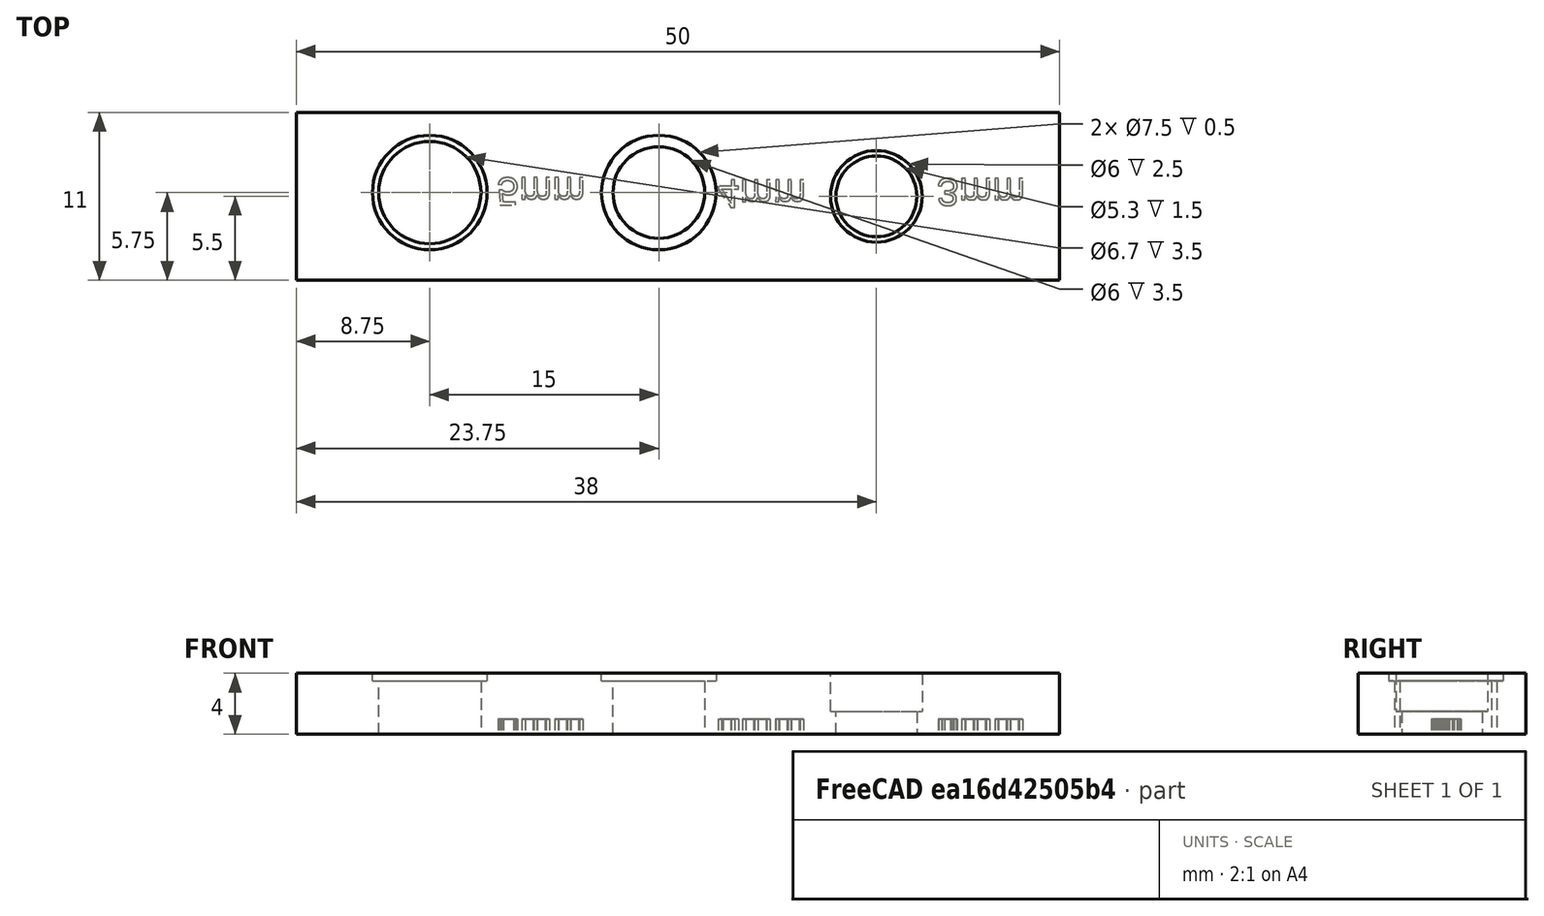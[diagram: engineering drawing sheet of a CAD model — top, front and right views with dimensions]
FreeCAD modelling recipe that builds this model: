
FCSTD DOCUMENT  (FreeCAD 0.17R13522 (Git))
Label: test_for_leds
License: CreativeCommons Attribution-ShareAlike
LicenseURL: http://creativecommons.org/licenses/by-sa/4.0/
objects: Part::Cut×6, Part::Feature×3, Part::Part2DObjectPython×3, Part::Extrusion×3, Part::Box×1
note: 16 computed .brp shape members not serialized (recipe doc carries the construction recipe); baked Part::Feature solids carry a one-line shape summary decoded from their .brp

FEATURE [Part::Box] Box  label="Cube"
  AttacherType = Attacher::AttachEngine3D
  Height = 4
  Length = 50
  Width = 11
FEATURE [Part::Feature] Fusion001001  label="perforador led 5 mm001"
  Placement = pos=(5,2,4) rot=(0,0,1;0rad)
  shape: bbox 7.5 x 7.5 x 10 mm, 13 faces (baked)
FEATURE [Part::Feature] Fusion001002  label="perforador led 4 mm001"
  Placement = pos=(20,2,4) rot=(0,0,1;0rad)
  shape: bbox 7.5 x 7.5 x 10 mm, 13 faces (baked)
FEATURE [Part::Feature] Fusion001003  label="perforador led 3 mm001"
  Placement = pos=(35,2.5,4) rot=(0,0,1;0rad)
  shape: bbox 6 x 6 x 10 mm, 13 faces (baked)
FEATURE [Part::Cut] Cut
  Base = -> Box
  Refine = true
  Tool = -> Fusion001001
FEATURE [Part::Cut] Cut001
  Base = -> Cut
  Refine = true
  Tool = -> Fusion001002
FEATURE [Part::Cut] Cut002
  Base = -> Cut001
  Refine = true
  Tool = -> Fusion001003
FEATURE [Part::Part2DObjectPython] ShapeString  # Draft 2D object (typed FeaturePython)
  FontFile = <path>
  Placement = pos=(41.94,6.68,0) rot=(1,0,0;3.14159rad)
  Size = 2
  String = 3mm
  Support = -> [Cut002]
  Tracking = 0
FEATURE [Part::Part2DObjectPython] ShapeString001  # Draft 2D object (typed FeaturePython)
  FontFile = <path>
  Placement = pos=(27.58,6.58,0) rot=(1,0,0;3.14159rad)
  Size = 2
  String = 4mm
  Tracking = 0
FEATURE [Part::Part2DObjectPython] ShapeString002  # Draft 2D object (typed FeaturePython)
  FontFile = <path>
  Placement = pos=(13.13,6.73,0) rot=(1,0,0;3.14159rad)
  Size = 2
  String = 5mm
  Tracking = 0
FEATURE [Part::Extrusion] Extrude
  Base = -> ShapeString002
  Dir = (0,0,-1)
  DirMode = 2
  FaceMakerClass = Part::FaceMakerBullseye
  LengthFwd = 1
  LengthRev = 0
  Placement = pos=(0,0,1) rot=(0,0,1;0rad)
  Solid = false
  Symmetric = false
FEATURE [Part::Extrusion] Extrude001
  Base = -> ShapeString001
  Dir = (0,0,-1)
  DirMode = 2
  FaceMakerClass = Part::FaceMakerBullseye
  LengthFwd = 1
  LengthRev = 0
  Placement = pos=(0,0,1) rot=(0,0,1;0rad)
  Solid = false
  Symmetric = false
FEATURE [Part::Extrusion] Extrude002
  Base = -> ShapeString
  Dir = (0,0,-1)
  DirMode = 2
  FaceMakerClass = Part::FaceMakerBullseye
  LengthFwd = 1
  LengthRev = 0
  Placement = pos=(0,0,1) rot=(0,0,1;0rad)
  Solid = false
  Symmetric = false
FEATURE [Part::Cut] Cut003
  Base = -> Cut002
  Refine = true
  Tool = -> Extrude002
FEATURE [Part::Cut] Cut004
  Base = -> Cut003
  Refine = true
  Tool = -> Extrude001
FEATURE [Part::Cut] Cut005
  Base = -> Cut004
  Refine = true
  Tool = -> Extrude
note: 3 file-system paths scrubbed to <path> (originals preserved in the JSON sidecar)
